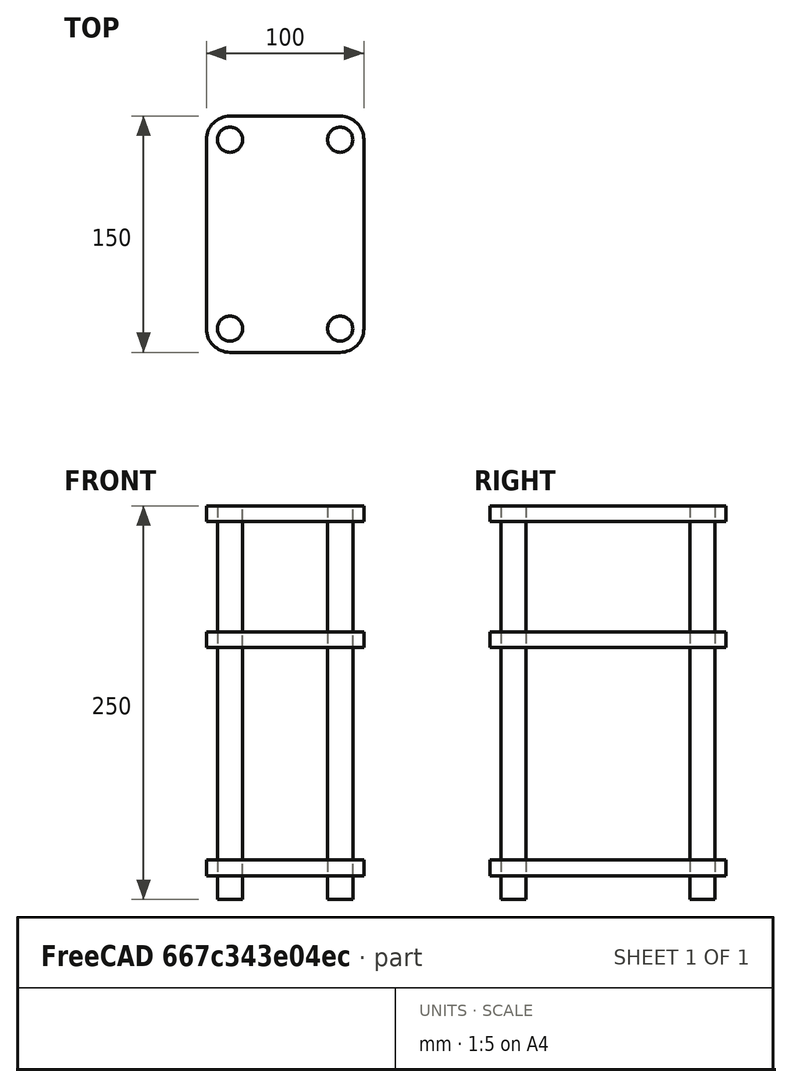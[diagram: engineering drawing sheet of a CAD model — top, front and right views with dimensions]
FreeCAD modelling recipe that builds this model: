
FCSTD DOCUMENT  (FreeCAD 1.0R38806 (Git))
Label: Mueble
License: All rights reserved
LicenseURL: http://en.wikipedia.org/wiki/All_rights_reserved
objects: Part::Cylinder×4, Part::Box×3, Part::Fillet×3
note: 10 computed .brp shape members not serialized (recipe doc carries the construction recipe); baked Part::Feature solids carry a one-line shape summary decoded from their .brp

FEATURE [Part::Box] Box  label="Balda1"
  AttacherType = Attacher::AttachEngine3D
  Height = 10
  Length = 100
  Width = 150
FEATURE [Part::Fillet] Fillet  label="BaldaRedondeada1"
  Base = -> Box
  EdgeLinks = -> Box [Edge1,Edge3,Edge5,Edge7]
  Edges = 4 edges r=15: [Edge1,Edge3,Edge5,Edge7]
  Placement = pos=(0,0,240) rot=(0,0,1;0rad)
FEATURE [Part::Box] Box001  label="Balda002"
  AttacherType = Attacher::AttachEngine3D
  Height = 10
  Length = 100
  Width = 150
FEATURE [Part::Fillet] Fillet001  label="BaldaRedondeada2"
  Base = -> Box001
  EdgeLinks = -> Box001 [Edge1,Edge3,Edge5,Edge7]
  Edges = 4 edges r=15: [Edge1,Edge3,Edge5,Edge7]
  Placement = pos=(0,0,160) rot=(0,0,1;0rad)
FEATURE [Part::Box] Box002  label="Balda003"
  AttacherType = Attacher::AttachEngine3D
  Height = 10
  Length = 100
  Width = 150
FEATURE [Part::Fillet] Fillet002  label="BaldaRedondeada3"
  Base = -> Box002
  EdgeLinks = -> Box002 [Edge1,Edge3,Edge5,Edge7]
  Edges = 4 edges r=15: [Edge1,Edge3,Edge5,Edge7]
  Placement = pos=(0,0,15) rot=(0,0,1;0rad)
FEATURE [Part::Cylinder] Cylinder  label="Pata1"
  Angle = 360
  AttacherType = Attacher::AttachEngine3D
  FirstAngle = 0
  Height = 250
  Placement = pos=(15,15,0) rot=(0,0,1;0rad)
  Radius = 8
  SecondAngle = 0
FEATURE [Part::Cylinder] Cylinder001  label="Pata002"
  Angle = 360
  AttacherType = Attacher::AttachEngine3D
  FirstAngle = 0
  Height = 250
  Placement = pos=(85,15,0) rot=(0,0,1;0rad)
  Radius = 8
  SecondAngle = 0
FEATURE [Part::Cylinder] Cylinder002  label="Pata003"
  Angle = 360
  AttacherType = Attacher::AttachEngine3D
  FirstAngle = 0
  Height = 250
  Placement = pos=(85,135,0) rot=(0,0,1;0rad)
  Radius = 8
  SecondAngle = 0
FEATURE [Part::Cylinder] Cylinder003  label="Pata004"
  Angle = 360
  AttacherType = Attacher::AttachEngine3D
  FirstAngle = 0
  Height = 250
  Placement = pos=(15,135,0) rot=(0,0,1;0rad)
  Radius = 8
  SecondAngle = 0
